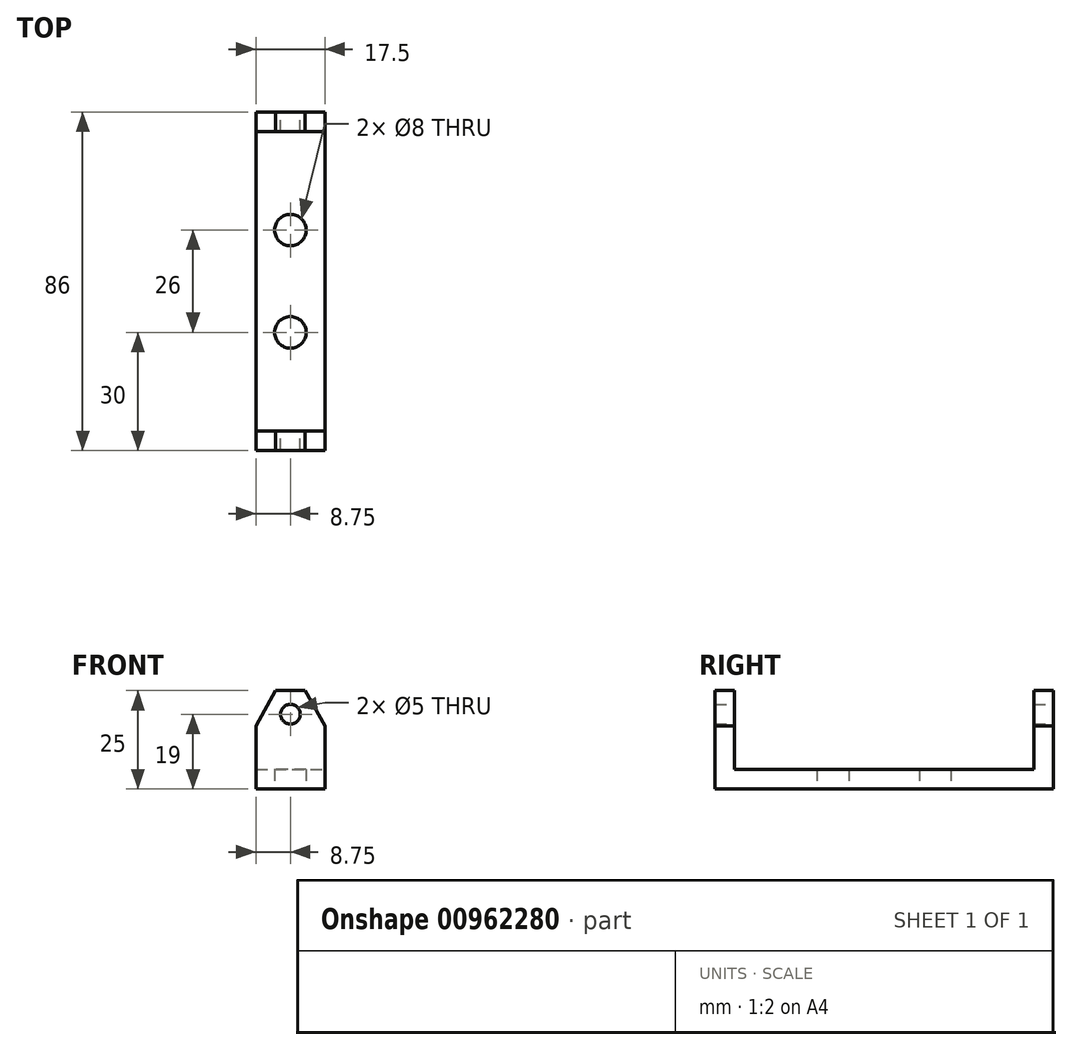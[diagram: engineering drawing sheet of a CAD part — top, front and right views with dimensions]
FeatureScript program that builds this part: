
annotation { "Feature Type Name" : "Feature", "Feature Type Description" : "" }
export const myFeature = defineFeature(function(context is Context, id is Id, definition is map)
    precondition{}
    {
        {
            var Q0;
            Q0=qCreatedBy(makeId("Top.planeOp"),FACE);
            var sketch = newSketch(context, id + "F0", { "sketchPlane" : qUnion([Q0])});
            skLineSegment(sketch, "E0.bottom", {"start": v(-8.75, 38) * mm, "end": v(8.75, 38) * mm});
            skLineSegment(sketch, "E0.top", {"start": v(-8.75, -38) * mm, "end": v(8.75, -38) * mm});
            skLineSegment(sketch, "E0.left", {"start": v(-8.75, 38) * mm, "end": v(-8.75, -38) * mm});
            skLineSegment(sketch, "E0.right", {"start": v(8.75, 38) * mm, "end": v(8.75, -38) * mm});
            skPoint(sketch, "E0.middle", {"position": v(0, 0) * mm});
            skLineSegment(sketch, "E1.top", {"start": v(-8.75, -43) * mm, "end": v(8.75, -43) * mm});
            skLineSegment(sketch, "E1.left", {"start": v(-8.75, -38) * mm, "end": v(-8.75, -43) * mm});
            skLineSegment(sketch, "E1.right", {"start": v(8.75, -38) * mm, "end": v(8.75, -43) * mm});
            skLineSegment(sketch, "E2.top", {"start": v(-8.75, 43) * mm, "end": v(8.75, 43) * mm});
            skLineSegment(sketch, "E2.left", {"start": v(-8.75, 38) * mm, "end": v(-8.75, 43) * mm});
            skLineSegment(sketch, "E2.right", {"start": v(8.75, 38) * mm, "end": v(8.75, 43) * mm});
            skCircle(sketch, "E3", {"center": v(0, 13) * mm, "radius": 4 * mm});
            skCircle(sketch, "E4", {"center": v(0, -13) * mm, "radius": 4 * mm});
            skSolve(sketch);
        }
        {
            var Q0;
            Q0=makeQuery(id+"F0.imprint","IMPRINT",FACE,{"disambiguationData":[TD([[makeQuery(id+"F0.imprint","IMPRINT",EDGE,{"derivedFrom":sQuery(id+"F0.wireOp",EDGE,"E0.left")}),1.0]])]});
            extrude(context, id + "F1", {"entities" : qUnion([Q0]), "depth" : 5 * mm, "offsetDistance" : 25 * mm});
        }
        {
            var Q0;
            Q0=makeQuery(id+"F0.imprint","IMPRINT",FACE,{"disambiguationData":[TD([[makeQuery(id+"F0.imprint","IMPRINT",EDGE,{"derivedFrom":sQuery(id+"F0.wireOp",EDGE,"E0.bottom")}),1.0]])]});
            var Q1;
            Q1=makeQuery(id+"F0.imprint","IMPRINT",FACE,{"disambiguationData":[TD([[makeQuery(id+"F0.imprint","IMPRINT",EDGE,{"derivedFrom":sQuery(id+"F0.wireOp",EDGE,"E0.top")}),-1.0]])]});
            extrude(context, id + "F2", {"entities" : qUnion([Q0, Q1]), "operationType" : NewBodyOperationType.ADD, "depth" : 25 * mm, "offsetDistance" : 25 * mm});
        }
        {
            var Q0;
            Q0=makeQuery(id+"F2.opExtrude","SWEPT_FACE",FACE,{"disambiguationData":[OSD([sQuery(id+"F0.wireOp",EDGE,"E2.top")])]});
            var sketch = newSketch(context, id + "F3", { "sketchPlane" : qUnion([Q0])});
            skLineSegment(sketch, "E5.0.0", {"start": v(-8.75, 0) * mm, "end": v(8.75, 0) * mm});
            skLineSegment(sketch, "E5.0.1", {"start": v(8.75, 0) * mm, "end": v(8.75, 25) * mm});
            skLineSegment(sketch, "E5.0.2", {"start": v(8.75, 25) * mm, "end": v(-8.75, 25) * mm});
            skLineSegment(sketch, "E5.0.3", {"start": v(-8.75, 25) * mm, "end": v(-8.75, 0) * mm});
            skPoint(sketch, "E6", {"position": v(-8.75, 16) * mm});
            skPoint(sketch, "E7", {"position": v(8.75, 16) * mm});
            skPoint(sketch, "E8", {"position": v(-3.75, 25) * mm});
            skPoint(sketch, "E9", {"position": v(3.75, 25) * mm});
            skLineSegment(sketch, "E10", {"start": v(-3.75, 25) * mm, "end": v(-8.75, 16) * mm});
            skLineSegment(sketch, "E11", {"start": v(3.75, 25) * mm, "end": v(8.75, 16) * mm});
            skCircle(sketch, "E12", {"center": v(0, 19) * mm, "radius": 2.5 * mm});
            skSolve(sketch);
        }
        {
            var Q0;
            {var subQ3=sQuery(id+"F3.wireOp",EDGE,"E11");Q0=makeQuery(id+"F3.imprint","IMPRINT",FACE,{"disambiguationData":[TD([[makeQuery(id+"F3.imprint","IMPRINT",EDGE,{"derivedFrom":subQ3}),1.0]])]});}
            var Q1;
            {var subQ3=sQuery(id+"F3.wireOp",EDGE,"E10");Q1=makeQuery(id+"F3.imprint","IMPRINT",FACE,{"disambiguationData":[TD([[makeQuery(id+"F3.imprint","IMPRINT",EDGE,{"derivedFrom":subQ3}),-1.0]])]});}
            var Q2;
            Q2=makeQuery(id+"F3.imprint","IMPRINT",FACE,{"disambiguationData":[TD([[makeQuery(id+"F3.imprint","IMPRINT",EDGE,{"derivedFrom":sQuery(id+"F3.wireOp",EDGE,"E12")}),1.0]])]});
            extrude(context, id + "F4", {"entities" : qUnion([Q0, Q1, Q2]), "operationType" : NewBodyOperationType.REMOVE, "oppositeDirection" : true, "depth" : 100 * mm, "offsetDistance" : 25 * mm});
        }
    });
